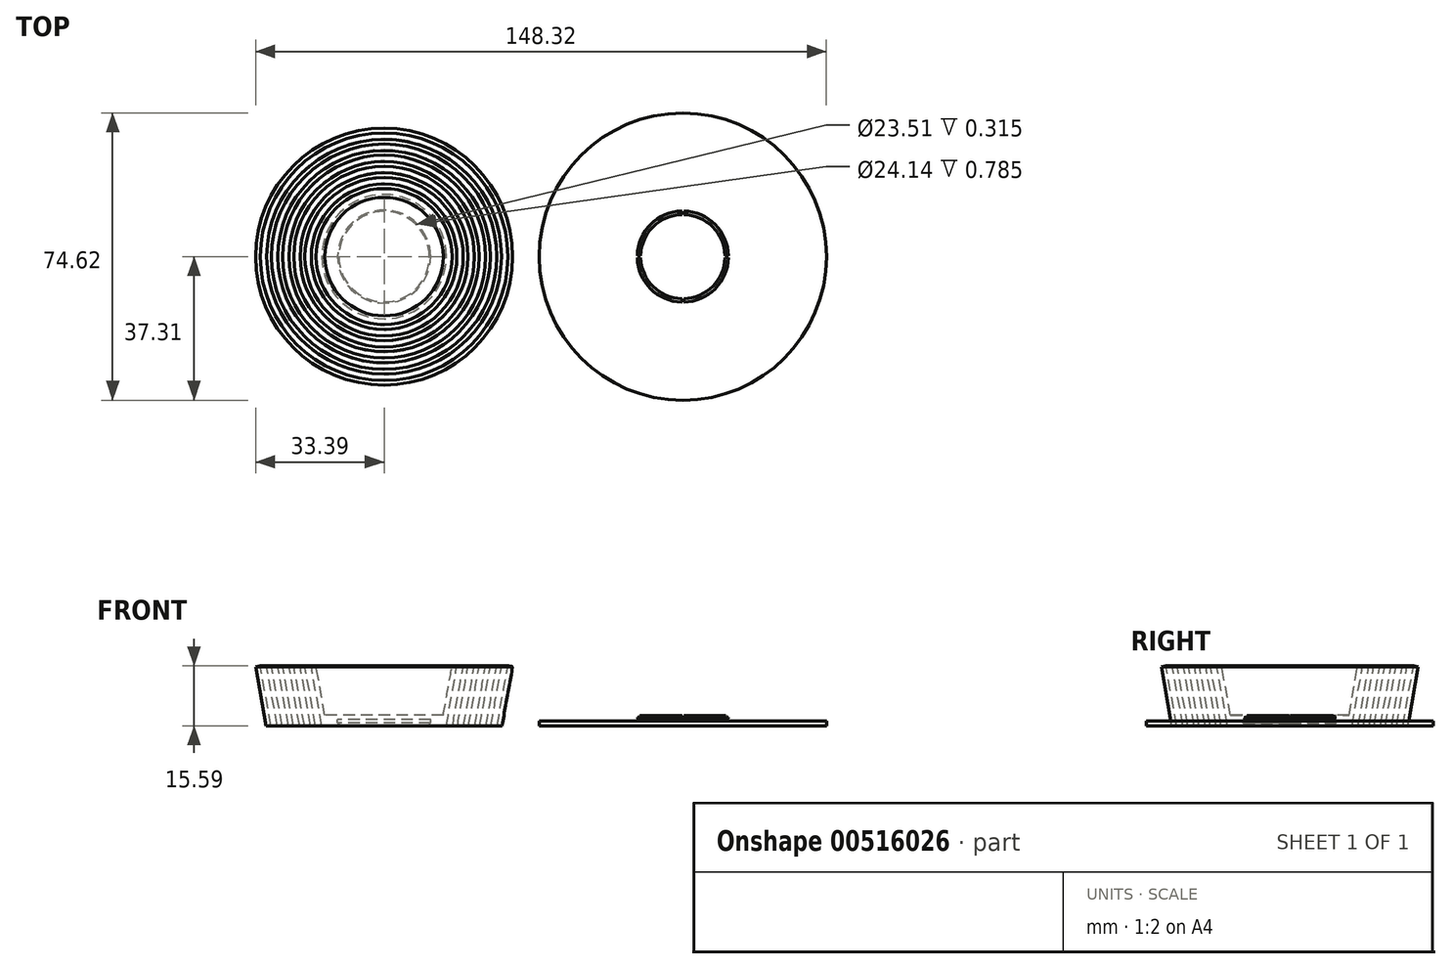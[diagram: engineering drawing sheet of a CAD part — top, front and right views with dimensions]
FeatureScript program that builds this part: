
annotation { "Feature Type Name" : "Feature", "Feature Type Description" : "" }
export const myFeature = defineFeature(function(context is Context, id is Id, definition is map)
    precondition{}
    {
        {
            var Q0;
            Q0=qCreatedBy(makeId("Front.planeOp"),FACE);
            var sketch = newSketch(context, id + "F0", { "sketchPlane" : qUnion([Q0])});
            skLineSegment(sketch, "E0", {"start": v(0, 0) * mm, "end": v(16.17, 0) * mm});
            skLineSegment(sketch, "E1", {"start": v(16.17, 0) * mm, "end": v(18.91, 15.37) * mm});
            skLineSegment(sketch, "E2", {"start": v(18.91, 15.37) * mm, "end": v(17.68, 15.59) * mm});
            skLineSegment(sketch, "E3", {"start": v(17.68, 15.59) * mm, "end": v(15.39, 2.76) * mm});
            skLineSegment(sketch, "E4", {"start": v(15.39, 2.76) * mm, "end": v(0, 2.76) * mm});
            skLineSegment(sketch, "E5", {"start": v(0, 2.76) * mm, "end": v(0, 0) * mm});
            skLineSegment(sketch, "E6", {"start": v(15.39, 2.76) * mm, "end": v(14.9, 0) * mm});
            skLineSegment(sketch, "E7", {"start": v(14.9, 0) * mm, "end": v(11.76, 0) * mm});
            skLineSegment(sketch, "E8", {"start": v(11.76, 0) * mm, "end": v(11.76, 0.78) * mm});
            skLineSegment(sketch, "E9", {"start": v(11.76, 0.78) * mm, "end": v(12.07, 0.78) * mm});
            skLineSegment(sketch, "E10", {"start": v(12.07, 0.78) * mm, "end": v(12.07, 1.57) * mm});
            skLineSegment(sketch, "E11", {"start": v(12.07, 1.57) * mm, "end": v(0, 1.57) * mm});
            skLineSegment(sketch, "E12", {"start": v(77.62, 0) * mm, "end": v(100.82, 0) * mm});
            skLineSegment(sketch, "E13", {"start": v(77.62, 0) * mm, "end": v(77.62, 1.27) * mm});
            skLineSegment(sketch, "E14", {"start": v(77.62, 1.27) * mm, "end": v(88.58, 1.27) * mm});
            skLineSegment(sketch, "E15", {"start": v(114.93, 1.27) * mm, "end": v(114.93, 0) * mm});
            skLineSegment(sketch, "E16", {"start": v(114.93, 0) * mm, "end": v(100.82, 0) * mm});
            skLineSegment(sketch, "E17", {"start": v(89.22, 1.27) * mm, "end": v(89.22, 1.82) * mm});
            skLineSegment(sketch, "E18", {"start": v(89.22, 1.82) * mm, "end": v(89.52, 1.82) * mm});
            skLineSegment(sketch, "E19", {"start": v(89.52, 1.82) * mm, "end": v(89.52, 2.6) * mm});
            skLineSegment(sketch, "E20", {"start": v(89.52, 2.6) * mm, "end": v(88.58, 2.6) * mm});
            skLineSegment(sketch, "E21", {"start": v(88.58, 2.6) * mm, "end": v(88.58, 1.27) * mm});
            skLineSegment(sketch, "E22.trimOffspring", {"start": v(89.22, 1.27) * mm, "end": v(100.82, 1.27) * mm});
            skLineSegment(sketch, "E23.trimOffspring", {"start": v(89.22, 1.27) * mm, "end": v(114.93, 1.27) * mm});
            skLineSegment(sketch, "E24.1.0.0", {"start": v(20.58, 15.59) * mm, "end": v(18.28, 2.76) * mm});
            skLineSegment(sketch, "E24.1.0.1", {"start": v(19.06, 0) * mm, "end": v(21.8, 15.37) * mm});
            skLineSegment(sketch, "E24.1.0.2", {"start": v(18.28, 2.76) * mm, "end": v(17.8, 0) * mm});
            skLineSegment(sketch, "E24.1.0.3", {"start": v(21.8, 15.37) * mm, "end": v(20.58, 15.59) * mm});
            skLineSegment(sketch, "E24.2.0.0", {"start": v(23.47, 15.59) * mm, "end": v(21.18, 2.76) * mm});
            skLineSegment(sketch, "E24.2.0.1", {"start": v(21.96, 0) * mm, "end": v(24.7, 15.37) * mm});
            skLineSegment(sketch, "E24.2.0.2", {"start": v(21.18, 2.76) * mm, "end": v(20.69, 0) * mm});
            skLineSegment(sketch, "E24.2.0.3", {"start": v(24.7, 15.37) * mm, "end": v(23.47, 15.59) * mm});
            skLineSegment(sketch, "E24.3.0.0", {"start": v(26.37, 15.59) * mm, "end": v(24.08, 2.76) * mm});
            skLineSegment(sketch, "E24.3.0.1", {"start": v(24.85, 0) * mm, "end": v(27.6, 15.37) * mm});
            skLineSegment(sketch, "E24.3.0.2", {"start": v(24.08, 2.76) * mm, "end": v(23.58, 0) * mm});
            skLineSegment(sketch, "E24.3.0.3", {"start": v(27.6, 15.37) * mm, "end": v(26.37, 15.59) * mm});
            skLineSegment(sketch, "E24.4.0.0", {"start": v(29.26, 15.59) * mm, "end": v(26.97, 2.76) * mm});
            skLineSegment(sketch, "E24.4.0.1", {"start": v(27.75, 0) * mm, "end": v(30.5, 15.37) * mm});
            skLineSegment(sketch, "E24.4.0.2", {"start": v(26.97, 2.76) * mm, "end": v(26.48, 0) * mm});
            skLineSegment(sketch, "E24.4.0.3", {"start": v(30.5, 15.37) * mm, "end": v(29.26, 15.59) * mm});
            skLineSegment(sketch, "E24.5.0.0", {"start": v(32.16, 15.59) * mm, "end": v(29.87, 2.76) * mm});
            skLineSegment(sketch, "E24.5.0.1", {"start": v(30.64, 0) * mm, "end": v(33.39, 15.37) * mm});
            skLineSegment(sketch, "E24.5.0.2", {"start": v(29.87, 2.76) * mm, "end": v(29.37, 0) * mm});
            skLineSegment(sketch, "E24.5.0.3", {"start": v(33.39, 15.37) * mm, "end": v(32.16, 15.59) * mm});
            skLineSegment(sketch, "E25", {"start": v(17.8, 0) * mm, "end": v(19.06, 0) * mm});
            skLineSegment(sketch, "E26", {"start": v(20.69, 0) * mm, "end": v(21.96, 0) * mm});
            skLineSegment(sketch, "E27", {"start": v(23.58, 0) * mm, "end": v(24.85, 0) * mm});
            skLineSegment(sketch, "E28", {"start": v(26.48, 0) * mm, "end": v(27.75, 0) * mm});
            skLineSegment(sketch, "E29", {"start": v(29.37, 0) * mm, "end": v(30.64, 0) * mm});
            skSolve(sketch);
        }
        {
            var Q0;
            {var subQ1=sQuery(id+"F0.wireOp",EDGE,"E4");Q0=makeQuery(id+"F0.imprint","IMPRINT",FACE,{"disambiguationData":[TD([[makeQuery(id+"F0.imprint","IMPRINT",EDGE,{"derivedFrom":subQ1}),1.0]])]});}
            var Q1;
            {var subQ0=sQuery(id+"F0.wireOp",EDGE,"E1");Q1=makeQuery(id+"F0.imprint","IMPRINT",FACE,{"disambiguationData":[TD([[makeQuery(id+"F0.imprint","IMPRINT",EDGE,{"derivedFrom":subQ0}),1.0]])]});}
            var Q2;
            Q2=makeQuery(id+"F0.imprint","IMPRINT",FACE,{"disambiguationData":[TD([[makeQuery(id+"F0.imprint","IMPRINT",EDGE,{"derivedFrom":sQuery(id+"F0.wireOp",EDGE,"962a1317-fa01-472c-be51-dec6157a52e8.1.0.0")}),1.0]])]});
            var Q3;
            Q3=makeQuery(id+"F0.imprint","IMPRINT",FACE,{"disambiguationData":[TD([[makeQuery(id+"F0.imprint","IMPRINT",EDGE,{"derivedFrom":sQuery(id+"F0.wireOp",EDGE,"962a1317-fa01-472c-be51-dec6157a52e8.2.0.0")}),1.0]])]});
            var Q4;
            Q4=makeQuery(id+"F0.imprint","IMPRINT",FACE,{"disambiguationData":[TD([[makeQuery(id+"F0.imprint","IMPRINT",EDGE,{"derivedFrom":sQuery(id+"F0.wireOp",EDGE,"962a1317-fa01-472c-be51-dec6157a52e8.3.0.0")}),1.0]])]});
            var Q5;
            Q5=makeQuery(id+"F0.imprint","IMPRINT",FACE,{"disambiguationData":[TD([[makeQuery(id+"F0.imprint","IMPRINT",EDGE,{"derivedFrom":sQuery(id+"F0.wireOp",EDGE,"962a1317-fa01-472c-be51-dec6157a52e8.4.0.0")}),1.0]])]});
            var Q6;
            Q6=makeQuery(id+"F0.imprint","IMPRINT",FACE,{"disambiguationData":[TD([[makeQuery(id+"F0.imprint","IMPRINT",EDGE,{"derivedFrom":sQuery(id+"F0.wireOp",EDGE,"962a1317-fa01-472c-be51-dec6157a52e8.5.0.0")}),1.0]])]});
            var Q7;
            Q7=makeQuery(id+"F0.imprint","IMPRINT",FACE,{"disambiguationData":[TD([[makeQuery(id+"F0.imprint","IMPRINT",EDGE,{"derivedFrom":sQuery(id+"F0.wireOp",EDGE,"E24.1.0.0")}),1.0]])]});
            var Q8;
            Q8=makeQuery(id+"F0.imprint","IMPRINT",FACE,{"disambiguationData":[TD([[makeQuery(id+"F0.imprint","IMPRINT",EDGE,{"derivedFrom":sQuery(id+"F0.wireOp",EDGE,"E24.2.0.0")}),1.0]])]});
            var Q9;
            Q9=makeQuery(id+"F0.imprint","IMPRINT",FACE,{"disambiguationData":[TD([[makeQuery(id+"F0.imprint","IMPRINT",EDGE,{"derivedFrom":sQuery(id+"F0.wireOp",EDGE,"E24.3.0.0")}),1.0]])]});
            var Q10;
            Q10=makeQuery(id+"F0.imprint","IMPRINT",FACE,{"disambiguationData":[TD([[makeQuery(id+"F0.imprint","IMPRINT",EDGE,{"derivedFrom":sQuery(id+"F0.wireOp",EDGE,"E24.4.0.0")}),1.0]])]});
            var Q11;
            Q11=makeQuery(id+"F0.imprint","IMPRINT",FACE,{"disambiguationData":[TD([[makeQuery(id+"F0.imprint","IMPRINT",EDGE,{"derivedFrom":sQuery(id+"F0.wireOp",EDGE,"E24.5.0.0")}),1.0]])]});
            var Q12;
            Q12=sQuery(id+"F0.wireOp",EDGE,"E5");
            revolve(context, id + "F1", {"entities" : qUnion([Q0, Q1, Q2, Q3, Q4, Q5, Q6, Q7, Q8, Q9, Q10, Q11]), "axis" : qUnion([Q12]), "revolveType" : RevolveType.FULL});
        }
        {
            var Q0;
            Q0=makeQuery(id+"F0.imprint","IMPRINT",FACE,{"disambiguationData":[TD([[makeQuery(id+"F0.imprint","IMPRINT",EDGE,{"derivedFrom":sQuery(id+"F0.wireOp",EDGE,"E12")}),1.0]])]});
            var Q1;
            Q1=sQuery(id+"F0.wireOp",EDGE,"E13");
            revolve(context, id + "F2", {"entities" : qUnion([Q0]), "axis" : qUnion([Q1]), "revolveType" : RevolveType.FULL});
        }
        {
            var Q0;
            Q0=makeQuery(id+"F2.opRevolve","SWEPT_FACE",FACE,{"disambiguationData":[OSD([sQuery(id+"F0.wireOp",EDGE,"E20")])]});
            var sketch = newSketch(context, id + "F3", { "sketchPlane" : qUnion([Q0])});
            skLineSegment(sketch, "E30.bottom", {"start": v(77.88, 12.97) * mm, "end": v(77.37, 12.97) * mm});
            skLineSegment(sketch, "E30.top", {"start": v(77.88, -12.97) * mm, "end": v(77.37, -12.97) * mm});
            skLineSegment(sketch, "E30.left", {"start": v(77.88, 12.97) * mm, "end": v(77.88, -12.97) * mm});
            skLineSegment(sketch, "E30.right", {"start": v(77.37, 12.97) * mm, "end": v(77.37, -12.97) * mm});
            skPoint(sketch, "E30.middle", {"position": v(77.62, 0) * mm});
            skLineSegment(sketch, "E31.bottom", {"start": v(94.17, 0.25) * mm, "end": v(61.08, 0.25) * mm});
            skLineSegment(sketch, "E31.top", {"start": v(94.17, -0.25) * mm, "end": v(61.08, -0.25) * mm});
            skLineSegment(sketch, "E31.left", {"start": v(94.17, 0.25) * mm, "end": v(94.17, -0.25) * mm});
            skLineSegment(sketch, "E31.right", {"start": v(61.08, 0.25) * mm, "end": v(61.08, -0.25) * mm});
            skSolve(sketch);
        }
        {
            var Q0;
            {var subQ0=sQuery(id+"F3.wireOp",EDGE,"E30.left");var subQ1=sQuery(id+"F0.wireOp",EDGE,"E20");var subQ2=makeQuery(id+"F2.opRevolve","SWEPT_EDGE",EDGE,{"disambiguationData":[OSD([sQuery(id+"F0.wireOp",EDGE,"E19"),subQ1])]});var subQ3=makeQuery(id+"F3.imprint","INTERSECT",VERTEX,{"disambiguationData":[OD(0.0)],"derivedFrom":[subQ2,subQ0]});Q0=makeQuery(id+"F3.imprint","IMPRINT",FACE,{"disambiguationData":[TD([[makeQuery(id+"F3.imprint","IMPRINT",EDGE,{"disambiguationData":[TD([[subQ3,-1.0]])],"derivedFrom":subQ0}),-1.0]])]});}
            var Q1;
            {var subQ0=sQuery(id+"F3.wireOp",EDGE,"E31.bottom");var subQ1=sQuery(id+"F0.wireOp",EDGE,"E20");var subQ2=makeQuery(id+"F2.opRevolve","SWEPT_EDGE",EDGE,{"disambiguationData":[OSD([sQuery(id+"F0.wireOp",EDGE,"E19"),subQ1])]});var subQ3=makeQuery(id+"F3.imprint","INTERSECT",VERTEX,{"disambiguationData":[OD(1.0)],"derivedFrom":[subQ2,subQ0]});Q1=makeQuery(id+"F3.imprint","IMPRINT",FACE,{"disambiguationData":[TD([[makeQuery(id+"F3.imprint","IMPRINT",EDGE,{"disambiguationData":[TD([[subQ3,1.0]])],"derivedFrom":subQ0}),1.0]])]});}
            var Q2;
            {var subQ0=sQuery(id+"F3.wireOp",EDGE,"E30.left");var subQ1=sQuery(id+"F0.wireOp",EDGE,"E20");var subQ2=makeQuery(id+"F2.opRevolve","SWEPT_EDGE",EDGE,{"disambiguationData":[OSD([sQuery(id+"F0.wireOp",EDGE,"E19"),subQ1])]});var subQ3=makeQuery(id+"F3.imprint","INTERSECT",VERTEX,{"disambiguationData":[OD(1.0)],"derivedFrom":[subQ2,subQ0]});Q2=makeQuery(id+"F3.imprint","IMPRINT",FACE,{"disambiguationData":[TD([[makeQuery(id+"F3.imprint","IMPRINT",EDGE,{"disambiguationData":[TD([[subQ3,1.0]])],"derivedFrom":subQ0}),-1.0]])]});}
            var Q3;
            {var subQ0=sQuery(id+"F3.wireOp",EDGE,"E31.bottom");var subQ1=sQuery(id+"F0.wireOp",EDGE,"E20");var subQ2=makeQuery(id+"F2.opRevolve","SWEPT_EDGE",EDGE,{"disambiguationData":[OSD([sQuery(id+"F0.wireOp",EDGE,"E19"),subQ1])]});var subQ3=makeQuery(id+"F3.imprint","INTERSECT",VERTEX,{"disambiguationData":[OD(0.0)],"derivedFrom":[subQ2,subQ0]});Q3=makeQuery(id+"F3.imprint","IMPRINT",FACE,{"disambiguationData":[TD([[makeQuery(id+"F3.imprint","IMPRINT",EDGE,{"disambiguationData":[TD([[subQ3,-1.0]])],"derivedFrom":subQ0}),1.0]])]});}
            var Q4;
            Q4=makeQuery(id+"F2.opRevolve","SWEPT_FACE",FACE,{"disambiguationData":[OSD([sQuery(id+"F0.wireOp",EDGE,"E23.trimOffspring")])]});
            extrude(context, id + "F4", {"entities" : qUnion([Q0, Q1, Q2, Q3]), "operationType" : NewBodyOperationType.REMOVE, "endBound" : BoundingType.UP_TO_SURFACE, "oppositeDirection" : true, "depth" : 25.4 * mm, "endBoundEntityFace" : qUnion([Q4]), "offsetDistance" : 25.4 * mm});
        }
        {
            var Q0;
            {var subQ0=sQuery(id+"F0.wireOp",EDGE,"E19");var subQ1=sQuery(id+"F0.wireOp",EDGE,"E20");var subQ2=sQuery(id+"F3.wireOp",EDGE,"E30.right");var subQ3=makeQuery(id+"F2.opRevolve","SWEPT_EDGE",EDGE,{"disambiguationData":[OSD([subQ0,subQ1])]});Q0=makeQuery(id+"F4.boolean.opBoolean","SPLIT",EDGE,{"disambiguationData":[TD([makeQuery(id+"F4.opExtrude","SWEPT_FACE",FACE,{"disambiguationData":[OSD([subQ2]),TDD([makeQuery(id+"F3.imprint","IMPRINT",EDGE,{"disambiguationData":[TD([[makeQuery(id+"F3.imprint","INTERSECT",VERTEX,{"disambiguationData":[OD(1.0)],"derivedFrom":[subQ3,subQ2]}),1.0]])],"derivedFrom":subQ2})])]})])],"derivedFrom":subQ3});}
            var Q1;
            {var subQ0=sQuery(id+"F0.wireOp",EDGE,"E18");var subQ2=sQuery(id+"F0.wireOp",EDGE,"E20");var subQ3=sQuery(id+"F0.wireOp",EDGE,"E19");var subQ4=makeQuery(id+"F2.opRevolve","SWEPT_EDGE",EDGE,{"disambiguationData":[OSD([subQ3,subQ2])]});var subQ6=sQuery(id+"F3.wireOp",EDGE,"E30.right");Q1=makeQuery(id+"F4.boolean.opBoolean","SPLIT",EDGE,{"disambiguationData":[TD([makeQuery(id+"F4.opExtrude","SWEPT_FACE",FACE,{"disambiguationData":[OSD([subQ6]),TDD([makeQuery(id+"F3.imprint","IMPRINT",EDGE,{"disambiguationData":[TD([[makeQuery(id+"F3.imprint","INTERSECT",VERTEX,{"disambiguationData":[OD(1.0)],"derivedFrom":[subQ4,subQ6]}),1.0]])],"derivedFrom":subQ6})])]})])],"derivedFrom":makeQuery(id+"F2.opRevolve","SWEPT_EDGE",EDGE,{"disambiguationData":[OSD([subQ0,subQ3])]})});}
            var Q2;
            {var subQ0=sQuery(id+"F0.wireOp",EDGE,"E19");var subQ1=sQuery(id+"F3.wireOp",EDGE,"E30.left");var subQ2=sQuery(id+"F0.wireOp",EDGE,"E20");var subQ3=makeQuery(id+"F2.opRevolve","SWEPT_EDGE",EDGE,{"disambiguationData":[OSD([subQ0,subQ2])]});Q2=makeQuery(id+"F4.boolean.opBoolean","SPLIT",EDGE,{"disambiguationData":[TD([makeQuery(id+"F4.opExtrude","SWEPT_FACE",FACE,{"disambiguationData":[OSD([subQ1]),TDD([makeQuery(id+"F3.imprint","IMPRINT",EDGE,{"disambiguationData":[TD([[makeQuery(id+"F3.imprint","INTERSECT",VERTEX,{"disambiguationData":[OD(1.0)],"derivedFrom":[subQ3,subQ1]}),1.0]])],"derivedFrom":subQ1})])]})])],"derivedFrom":subQ3});}
            var Q3;
            {var subQ0=sQuery(id+"F0.wireOp",EDGE,"E18");var subQ1=sQuery(id+"F0.wireOp",EDGE,"E19");var subQ2=sQuery(id+"F3.wireOp",EDGE,"E30.left");var subQ3=sQuery(id+"F0.wireOp",EDGE,"E20");var subQ4=makeQuery(id+"F2.opRevolve","SWEPT_EDGE",EDGE,{"disambiguationData":[OSD([subQ1,subQ3])]});Q3=makeQuery(id+"F4.boolean.opBoolean","SPLIT",EDGE,{"disambiguationData":[TD([makeQuery(id+"F4.opExtrude","SWEPT_FACE",FACE,{"disambiguationData":[OSD([subQ2]),TDD([makeQuery(id+"F3.imprint","IMPRINT",EDGE,{"disambiguationData":[TD([[makeQuery(id+"F3.imprint","INTERSECT",VERTEX,{"disambiguationData":[OD(1.0)],"derivedFrom":[subQ4,subQ2]}),1.0]])],"derivedFrom":subQ2})])]})])],"derivedFrom":makeQuery(id+"F2.opRevolve","SWEPT_EDGE",EDGE,{"disambiguationData":[OSD([subQ0,subQ1])]})});}
            var Q4;
            {var subQ0=sQuery(id+"F0.wireOp",EDGE,"E19");var subQ1=sQuery(id+"F0.wireOp",EDGE,"E20");var subQ2=sQuery(id+"F3.wireOp",EDGE,"E30.left");var subQ3=makeQuery(id+"F2.opRevolve","SWEPT_EDGE",EDGE,{"disambiguationData":[OSD([subQ0,subQ1])]});Q4=makeQuery(id+"F4.boolean.opBoolean","SPLIT",EDGE,{"disambiguationData":[TD([makeQuery(id+"F4.opExtrude","SWEPT_FACE",FACE,{"disambiguationData":[OSD([subQ2]),TDD([makeQuery(id+"F3.imprint","IMPRINT",EDGE,{"disambiguationData":[TD([[makeQuery(id+"F3.imprint","INTERSECT",VERTEX,{"disambiguationData":[OD(0.0)],"derivedFrom":[subQ3,subQ2]}),-1.0]])],"derivedFrom":subQ2})])]})])],"derivedFrom":subQ3});}
            var Q5;
            {var subQ0=sQuery(id+"F0.wireOp",EDGE,"E19");var subQ1=sQuery(id+"F0.wireOp",EDGE,"E20");var subQ3=makeQuery(id+"F2.opRevolve","SWEPT_EDGE",EDGE,{"disambiguationData":[OSD([subQ0,subQ1])]});var subQ5=sQuery(id+"F3.wireOp",EDGE,"E30.right");Q5=makeQuery(id+"F4.boolean.opBoolean","SPLIT",EDGE,{"disambiguationData":[TD([makeQuery(id+"F4.opExtrude","SWEPT_FACE",FACE,{"disambiguationData":[OSD([subQ5]),TDD([makeQuery(id+"F3.imprint","IMPRINT",EDGE,{"disambiguationData":[TD([[makeQuery(id+"F3.imprint","INTERSECT",VERTEX,{"disambiguationData":[OD(0.0)],"derivedFrom":[subQ3,subQ5]}),-1.0]])],"derivedFrom":subQ5})])]})])],"derivedFrom":subQ3});}
            var Q6;
            {var subQ0=sQuery(id+"F0.wireOp",EDGE,"E18");var subQ2=sQuery(id+"F0.wireOp",EDGE,"E20");var subQ3=sQuery(id+"F0.wireOp",EDGE,"E19");var subQ4=makeQuery(id+"F2.opRevolve","SWEPT_EDGE",EDGE,{"disambiguationData":[OSD([subQ3,subQ2])]});var subQ6=sQuery(id+"F3.wireOp",EDGE,"E30.left");Q6=makeQuery(id+"F4.boolean.opBoolean","SPLIT",EDGE,{"disambiguationData":[TD([makeQuery(id+"F4.opExtrude","SWEPT_FACE",FACE,{"disambiguationData":[OSD([subQ6]),TDD([makeQuery(id+"F3.imprint","IMPRINT",EDGE,{"disambiguationData":[TD([[makeQuery(id+"F3.imprint","INTERSECT",VERTEX,{"disambiguationData":[OD(0.0)],"derivedFrom":[subQ4,subQ6]}),-1.0]])],"derivedFrom":subQ6})])]})])],"derivedFrom":makeQuery(id+"F2.opRevolve","SWEPT_EDGE",EDGE,{"disambiguationData":[OSD([subQ0,subQ3])]})});}
            var Q7;
            {var subQ0=sQuery(id+"F0.wireOp",EDGE,"E18");var subQ1=sQuery(id+"F0.wireOp",EDGE,"E19");var subQ2=sQuery(id+"F3.wireOp",EDGE,"E30.right");var subQ3=sQuery(id+"F0.wireOp",EDGE,"E20");var subQ4=makeQuery(id+"F2.opRevolve","SWEPT_EDGE",EDGE,{"disambiguationData":[OSD([subQ1,subQ3])]});Q7=makeQuery(id+"F4.boolean.opBoolean","SPLIT",EDGE,{"disambiguationData":[TD([makeQuery(id+"F4.opExtrude","SWEPT_FACE",FACE,{"disambiguationData":[OSD([subQ2]),TDD([makeQuery(id+"F3.imprint","IMPRINT",EDGE,{"disambiguationData":[TD([[makeQuery(id+"F3.imprint","INTERSECT",VERTEX,{"disambiguationData":[OD(0.0)],"derivedFrom":[subQ4,subQ2]}),-1.0]])],"derivedFrom":subQ2})])]})])],"derivedFrom":makeQuery(id+"F2.opRevolve","SWEPT_EDGE",EDGE,{"disambiguationData":[OSD([subQ0,subQ1])]})});}
            fillet(context, id + "F5", {"entities" : qUnion([Q0, Q1, Q2, Q3, Q4, Q5, Q6, Q7]), "radius" : 0.76 * mm, "tangentPropagation" : true, "allowEdgeOverflow" : false});
        }
        {
            var Q0;
            Q0=makeQuery(id+"F1.opRevolve","SWEPT_EDGE",EDGE,{"disambiguationData":[OSD([sQuery(id+"F0.wireOp",EDGE,"E8"),sQuery(id+"F0.wireOp",EDGE,"E9")])]});
            fillet(context, id + "F6", {"entities" : qUnion([Q0]), "radius" : 0.5 * mm, "tangentPropagation" : true, "allowEdgeOverflow" : false});
        }
    });
